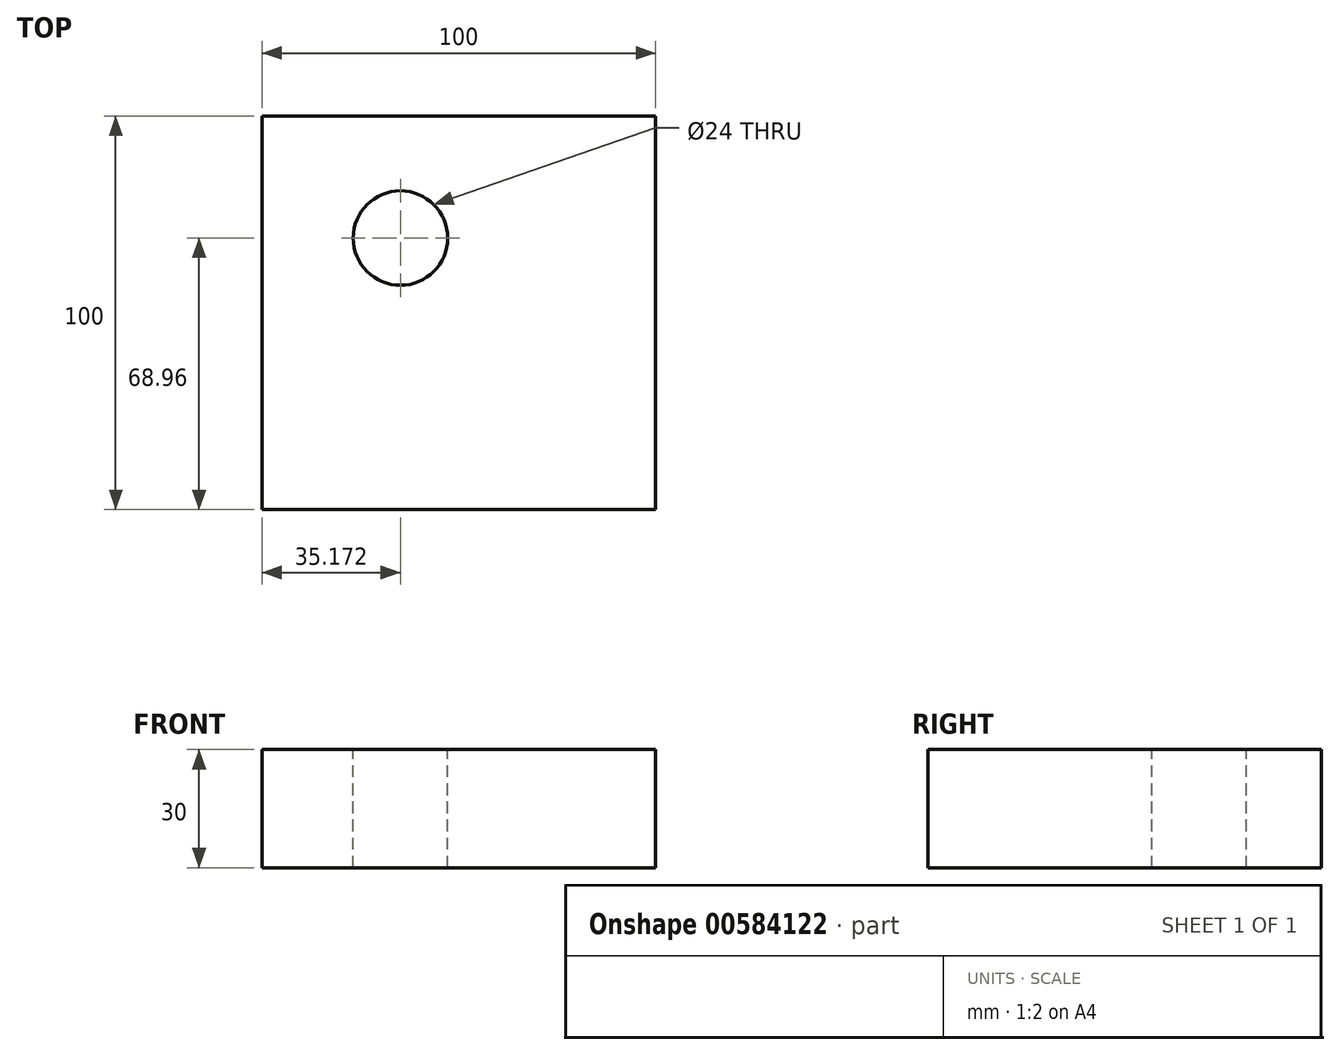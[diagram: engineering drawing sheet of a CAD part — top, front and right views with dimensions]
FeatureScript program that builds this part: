
annotation { "Feature Type Name" : "Feature", "Feature Type Description" : "" }
export const myFeature = defineFeature(function(context is Context, id is Id, definition is map)
    precondition{}
    {
        {
            var Q0;
            Q0=qCreatedBy(makeId("Top.planeOp"),FACE);
            var sketch = newSketch(context, id + "F0", { "sketchPlane" : qUnion([Q0])});
            skLineSegment(sketch, "E0.bottom", {"start": v(-53.75, 54.79) * mm, "end": v(46.25, 54.79) * mm});
            skLineSegment(sketch, "E0.top", {"start": v(-53.75, -45.21) * mm, "end": v(46.25, -45.21) * mm});
            skLineSegment(sketch, "E0.left", {"start": v(-53.75, 54.79) * mm, "end": v(-53.75, -45.21) * mm});
            skLineSegment(sketch, "E0.right", {"start": v(46.25, 54.79) * mm, "end": v(46.25, -45.21) * mm});
            skSolve(sketch);
        }
        {
            var Q0;
            Q0=makeQuery(id+"F0.imprint","IMPRINT",FACE,{"disambiguationData":[TD([[makeQuery(id+"F0.imprint","IMPRINT",EDGE,{"derivedFrom":sQuery(id+"F0.wireOp",EDGE,"E0.bottom")}),-1.0]])]});
            extrude(context, id + "F1", {"entities" : qUnion([Q0]), "depth" : 30 * mm, "offsetDistance" : 25 * mm});
        }
        {
            var Q0;
            Q0=makeQuery(id+"F1.opExtrude","CAP_FACE",FACE,{"disambiguationData":[OSD([sQuery(id+"F0.wireOp",EDGE,"E0.bottom"),sQuery(id+"F0.wireOp",EDGE,"E0.top"),sQuery(id+"F0.wireOp",EDGE,"E0.left"),sQuery(id+"F0.wireOp",EDGE,"E0.right")])],"isStart":false});
            var sketch = newSketch(context, id + "F2", { "sketchPlane" : qUnion([Q0])});
            skCircle(sketch, "E1", {"center": v(-18.58, 23.75) * mm, "radius": 12 * mm});
            skSolve(sketch);
        }
        {
            var Q0;
            Q0=makeQuery(id+"F2.imprint","IMPRINT",FACE,{"disambiguationData":[TD([[makeQuery(id+"F2.imprint","IMPRINT",EDGE,{"derivedFrom":sQuery(id+"F2.wireOp",EDGE,"E1")}),1.0]])]});
            var Q1;
            Q1=sQuery(id+"F2.wireOp",EDGE,"E1");
            extrude(context, id + "F3", {"entities" : qUnion([Q0]), "operationType" : NewBodyOperationType.REMOVE, "surfaceEntities" : qUnion([Q1]), "endBound" : BoundingType.THROUGH_ALL, "oppositeDirection" : true, "depth" : 99 * mm, "offsetDistance" : 25 * mm});
        }
    });
